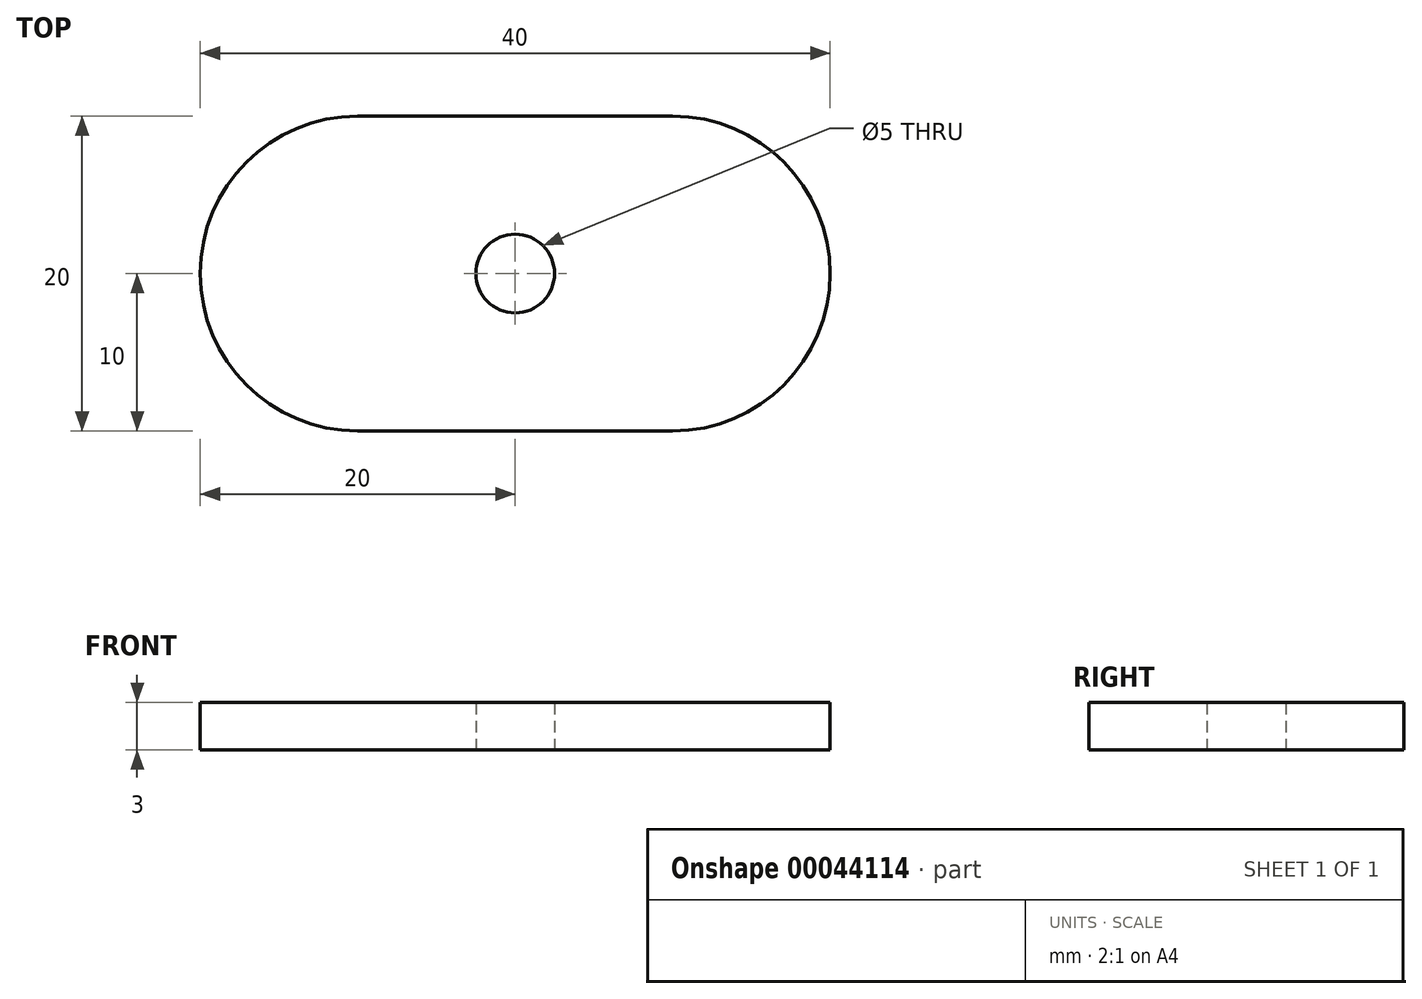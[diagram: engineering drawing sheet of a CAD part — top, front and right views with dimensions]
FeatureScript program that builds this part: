
annotation { "Feature Type Name" : "Feature", "Feature Type Description" : "" }
export const myFeature = defineFeature(function(context is Context, id is Id, definition is map)
    precondition{}
    {
        {
            var Q0;
            Q0=qCreatedBy(makeId("Top.planeOp"),FACE);
            var sketch = newSketch(context, id + "F0", { "sketchPlane" : qUnion([Q0])});
            skLineSegment(sketch, "E0.rect.bottom", {"start": v(10, -10) * mm, "end": v(-10, -10) * mm});
            skLineSegment(sketch, "E0.rect.top", {"start": v(10, 10) * mm, "end": v(-10, 10) * mm});
            skLineSegment(sketch, "E0.rect.left", {"start": v(10, -10) * mm, "end": v(10, 10) * mm});
            skLineSegment(sketch, "E0.rect.right", {"start": v(-10, -10) * mm, "end": v(-10, 10) * mm});
            skPoint(sketch, "E0.rect.middle", {"position": v(0, 0) * mm});
            skArc(sketch, "E1", {"start": v(-10, 10) * mm, "mid": v(-20, 0) * mm, "end": v(-10, -10) * mm});
            skArc(sketch, "E2", {"start": v(10, -10) * mm, "mid": v(20, 0) * mm, "end": v(10, 10) * mm});
            skCircle(sketch, "E3", {"center": v(0, 0) * mm, "radius": 2.5 * mm});
            skSolve(sketch);
        }
        {
            var Q0;
            Q0=makeQuery(id+"F0.imprint","IMPRINT",FACE,{"disambiguationData":[TD([[makeQuery(id+"F0.imprint","IMPRINT",EDGE,{"derivedFrom":sQuery(id+"F0.wireOp",EDGE,"E0.rect.right")}),1.0]])]});
            var Q1;
            Q1=makeQuery(id+"F0.imprint","IMPRINT",FACE,{"disambiguationData":[TD([[makeQuery(id+"F0.imprint","IMPRINT",EDGE,{"derivedFrom":sQuery(id+"F0.wireOp",EDGE,"E0.rect.bottom")}),-1.0]])]});
            var Q2;
            Q2=makeQuery(id+"F0.imprint","IMPRINT",FACE,{"disambiguationData":[TD([[makeQuery(id+"F0.imprint","IMPRINT",EDGE,{"derivedFrom":sQuery(id+"F0.wireOp",EDGE,"E0.rect.left")}),-1.0]])]});
            extrude(context, id + "F1", {"entities" : qUnion([Q0, Q1, Q2]), "depth" : 3 * mm});
        }
    });
